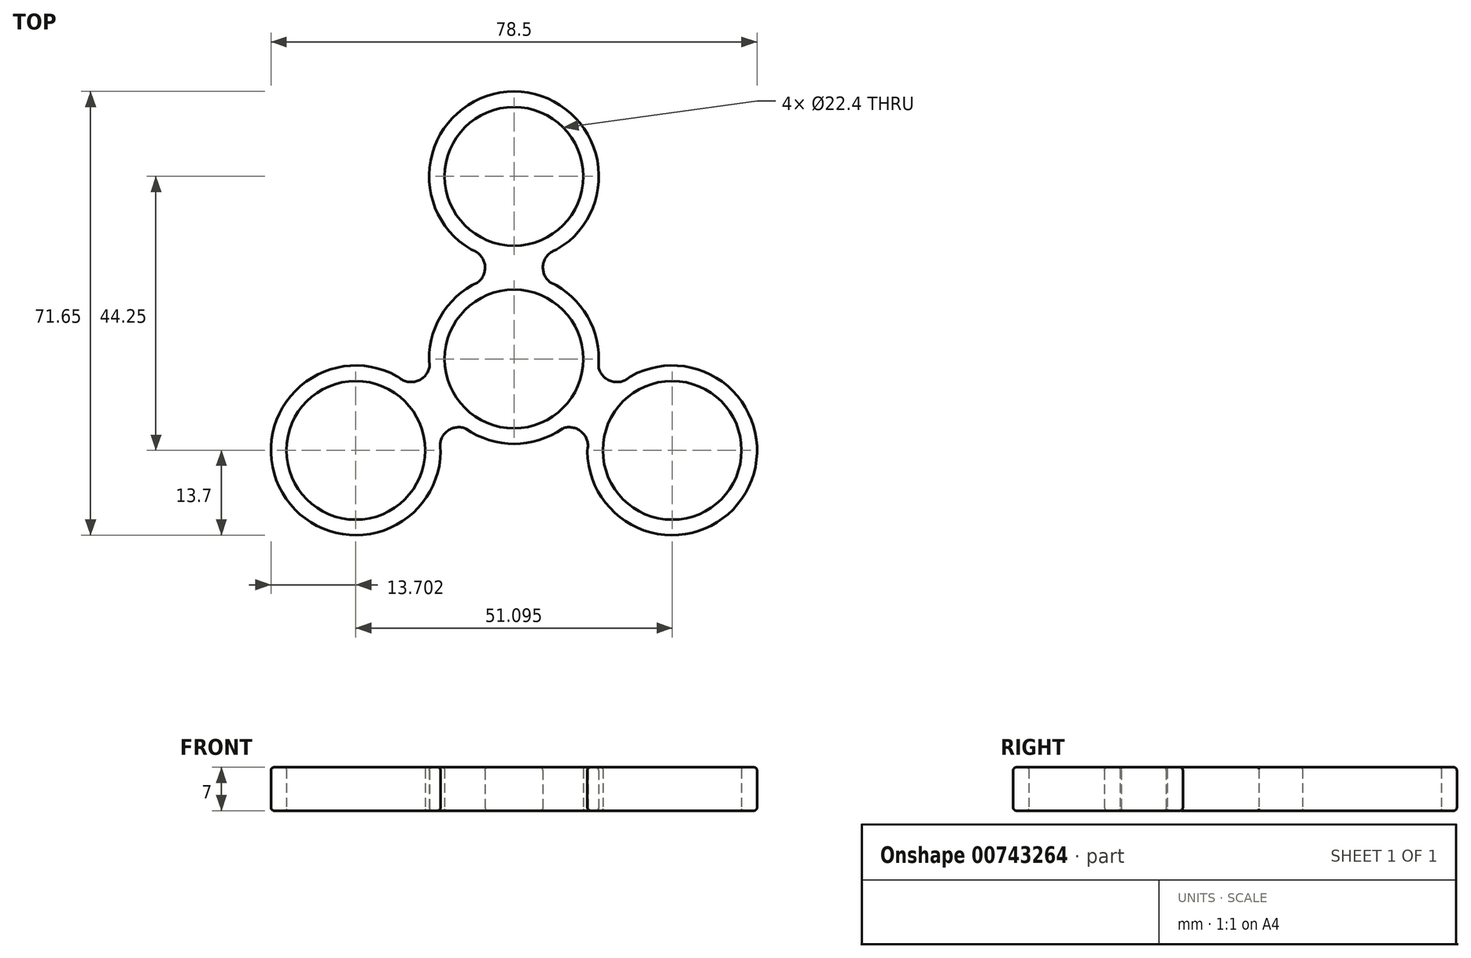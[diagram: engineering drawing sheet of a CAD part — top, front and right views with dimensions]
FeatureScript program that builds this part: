
annotation { "Feature Type Name" : "Feature", "Feature Type Description" : "" }
export const myFeature = defineFeature(function(context is Context, id is Id, definition is map)
    precondition{}
    {
        {
            var Q0;
            Q0=qCreatedBy(makeId("Top.planeOp"),FACE);
            var sketch = newSketch(context, id + "F0", { "sketchPlane" : qUnion([Q0])});
            skCircle(sketch, "E0", {"center": v(0, 0) * mm, "radius": 11.2 * mm});
            skArc(sketch, "E1.0", {"start": v(-5.2, 12.68) * mm, "mid": v(-5.5, 12.55) * mm, "end": v(-5.79, 12.42) * mm, "construction": true});
            skLineSegment(sketch, "E2", {"start": v(0, 0) * mm, "end": v(0, 29.5) * mm, "construction": true});
            skCircle(sketch, "E3", {"center": v(0, 29.5) * mm, "radius": 11.2 * mm});
            skArc(sketch, "E4.0", {"start": v(7, 17.72) * mm, "mid": v(0, 43.2) * mm, "end": v(-7, 17.72) * mm});
            skPoint(sketch, "E5.visualSharp", {"position": v(0, 14.75) * mm});
            skLineSegment(sketch, "E6.0", {"start": v(7, 0) * mm, "end": v(7, 29.5) * mm, "construction": true});
            skLineSegment(sketch, "E7", {"start": v(7, 17.72) * mm, "end": v(6.5, 17.51) * mm});
            skLineSegment(sketch, "E8", {"start": v(6.5, 11.99) * mm, "end": v(7, 11.78) * mm});
            skArc(sketch, "E9.filletArc", {"start": v(6.5, 17.51) * mm, "mid": v(4.67, 14.75) * mm, "end": v(6.5, 11.99) * mm});
            skLineSegment(sketch, "E10.MirrorCS", {"start": v(-7, 17.72) * mm, "end": v(-6.5, 17.51) * mm});
            skLineSegment(sketch, "E11.MirrorCS", {"start": v(-6.5, 11.99) * mm, "end": v(-7, 11.78) * mm});
            skArc(sketch, "E12.MirrorCS", {"start": v(-6.5, 17.51) * mm, "mid": v(-4.67, 14.75) * mm, "end": v(-6.5, 11.99) * mm});
            skArc(sketch, "E13.trimOffspring", {"start": v(-7, 11.78) * mm, "mid": v(0, -13.7) * mm, "end": v(7, 11.78) * mm});
            skSolve(sketch);
        }
        {
            var Q0;
            Q0=qSketchRegion(id+"F2",true);
            var Q1;
            Q1=qSketchRegion(id+"F0",true);
            extrude(context, id + "F1", {"entities" : qUnion([Q0, Q1]), "depth" : 7 * mm, "offsetDistance" : 25 * mm});
        }
        {
            var Q0;
            Q0=qCreatedBy(makeId("Right.planeOp"),FACE);
            var sketch = newSketch(context, id + "F2", { "sketchPlane" : qUnion([Q0])});
            skLineSegment(sketch, "E14", {"start": v(0, -11.35) * mm, "end": v(0, 14.45) * mm, "construction": true});
            skSolve(sketch);
        }
        {
            var Q0;
            Q0=makeQuery(id+"F1.opExtrude","SWEPT_BODY",BODY,{"disambiguationData":[OSD([sQuery(id+"F0.wireOp",EDGE,"E0"),sQuery(id+"F0.wireOp",EDGE,"E1.0"),sQuery(id+"F0.wireOp",EDGE,"E3"),sQuery(id+"F0.wireOp",EDGE,"E4.0"),sQuery(id+"F0.wireOp",EDGE,"7c884c8c-e37f-41f7-9a8e-9150e4511ce8.0"),sQuery(id+"F0.wireOp",EDGE,"124d70be-8a2f-4ff1-8067-023c3a760d13.0"),sQuery(id+"F0.wireOp",EDGE,"7qioyo7K-iHsX-Xa6s-X97m-BwtuQXfGrCvp"),sQuery(id+"F0.wireOp",EDGE,"oFAU7C9Q-nsB6-dseo-MMuZ-7hNLlDQCrwbt"),sQuery(id+"F0.wireOp",EDGE,"a2486781-22df-47b1-8026-fe576fbc433f.0"),sQuery(id+"F0.wireOp",EDGE,"cb9c9ce2-17e4-408e-8bf5-b38f411324f0.0"),sQuery(id+"F0.wireOp",EDGE,"jKmUo85i-UXFQ-YKQP-mafa-QPdGbBQ2pSZu"),sQuery(id+"F0.wireOp",EDGE,"14rnQz0T-OoW9-SuH9-BmvN-4Fd0IeYT7QfG")])]});
            var Q1;
            Q1=sQuery(id+"F2.wireOp",EDGE,"E14");
            circularPattern(context, id + "F3", {"operationType" : NewBodyOperationType.ADD, "entities" : qUnion([Q0]), "axis" : qUnion([Q1]), "angle" : 360 * degree, "instanceCount" : 3, "equalSpace" : true});
        }
        {
            var Q0;
            {var subQ0=makeQuery(id+"F1.opExtrude","SWEPT_FACE",FACE,{"disambiguationData":[OSD([sQuery(id+"F0.wireOp",EDGE,"E13.trimOffspring")])]});Q0=makeQuery(id+"F3.boolean.opBoolean","MERGE",FACE,{"disambiguationData":[OD(1.0)],"derivedFrom":[subQ0,makeQuery(id+"F3.opPattern","COPY",FACE,{"derivedFrom":subQ0,"instanceName":"1"}),makeQuery(id+"F3.opPattern","COPY",FACE,{"derivedFrom":subQ0,"instanceName":"2"})]});}
            var Q1;
            Q1=makeQuery(id+"F3.opPattern","COPY",FACE,{"derivedFrom":makeQuery(id+"F1.opExtrude","SWEPT_FACE",FACE,{"disambiguationData":[OSD([sQuery(id+"F0.wireOp",EDGE,"E4.0")])]}),"instanceName":"1"});
            var Q2;
            Q2=makeQuery(id+"F3.boolean.opBoolean","SPLIT",FACE,{"derivedFrom":makeQuery(id+"F1.opExtrude","SWEPT_FACE",FACE,{"disambiguationData":[OSD([sQuery(id+"F0.wireOp",EDGE,"E13.trimOffspring")])]})});
            var Q3;
            Q3=makeQuery(id+"F3.opPattern","COPY",FACE,{"derivedFrom":makeQuery(id+"F1.opExtrude","SWEPT_FACE",FACE,{"disambiguationData":[OSD([sQuery(id+"F0.wireOp",EDGE,"E12.MirrorCS")])]}),"instanceName":"1"});
            var Q4;
            Q4=makeQuery(id+"F3.opPattern","COPY",FACE,{"derivedFrom":makeQuery(id+"F1.opExtrude","SWEPT_FACE",FACE,{"disambiguationData":[OSD([sQuery(id+"F0.wireOp",EDGE,"E9.filletArc")])]}),"instanceName":"1"});
            var Q5;
            Q5=makeQuery(id+"F3.opPattern","COPY",FACE,{"derivedFrom":makeQuery(id+"F1.opExtrude","SWEPT_FACE",FACE,{"disambiguationData":[OSD([sQuery(id+"F0.wireOp",EDGE,"E9.filletArc")])]}),"instanceName":"2"});
            var Q6;
            Q6=makeQuery(id+"F3.opPattern","COPY",FACE,{"derivedFrom":makeQuery(id+"F1.opExtrude","SWEPT_FACE",FACE,{"disambiguationData":[OSD([sQuery(id+"F0.wireOp",EDGE,"E4.0")])]}),"instanceName":"2"});
            var Q7;
            Q7=makeQuery(id+"F3.opPattern","COPY",FACE,{"derivedFrom":makeQuery(id+"F1.opExtrude","SWEPT_FACE",FACE,{"disambiguationData":[OSD([sQuery(id+"F0.wireOp",EDGE,"E12.MirrorCS")])]}),"instanceName":"2"});
            var Q8;
            {var subQ0=makeQuery(id+"F1.opExtrude","SWEPT_FACE",FACE,{"disambiguationData":[OSD([sQuery(id+"F0.wireOp",EDGE,"E13.trimOffspring")])]});Q8=makeQuery(id+"F3.boolean.opBoolean","MERGE",FACE,{"disambiguationData":[OD(0.0)],"derivedFrom":[subQ0,makeQuery(id+"F3.opPattern","COPY",FACE,{"derivedFrom":subQ0,"instanceName":"1"}),makeQuery(id+"F3.opPattern","COPY",FACE,{"derivedFrom":subQ0,"instanceName":"2"})]});}
            var Q9;
            Q9=makeQuery(id+"F1.opExtrude","SWEPT_FACE",FACE,{"disambiguationData":[OSD([sQuery(id+"F0.wireOp",EDGE,"E9.filletArc")])]});
            var Q10;
            Q10=makeQuery(id+"F1.opExtrude","SWEPT_FACE",FACE,{"disambiguationData":[OSD([sQuery(id+"F0.wireOp",EDGE,"E4.0")])]});
            var Q11;
            Q11=makeQuery(id+"F1.opExtrude","SWEPT_FACE",FACE,{"disambiguationData":[OSD([sQuery(id+"F0.wireOp",EDGE,"E12.MirrorCS")])]});
            fillet(context, id + "F4", {"entities" : qUnion([Q0, Q1, Q2, Q3, Q4, Q5, Q6, Q7, Q8, Q9, Q10, Q11]), "radius" : 0.5 * mm, "tangentPropagation" : true, "allowEdgeOverflow" : false});
        }
        {
            var Q0;
            Q0=makeQuery(id+"F1.opExtrude","SWEPT_FACE",FACE,{"disambiguationData":[OSD([sQuery(id+"F0.wireOp",EDGE,"E3")])]});
            var Q1;
            Q1=makeQuery(id+"F1.opExtrude","SWEPT_FACE",FACE,{"disambiguationData":[OSD([sQuery(id+"F0.wireOp",EDGE,"E0")])]});
            var Q2;
            Q2=makeQuery(id+"F3.opPattern","COPY",FACE,{"derivedFrom":makeQuery(id+"F1.opExtrude","SWEPT_FACE",FACE,{"disambiguationData":[OSD([sQuery(id+"F0.wireOp",EDGE,"E3")])]}),"instanceName":"2"});
            var Q3;
            Q3=makeQuery(id+"F3.opPattern","COPY",FACE,{"derivedFrom":makeQuery(id+"F1.opExtrude","SWEPT_FACE",FACE,{"disambiguationData":[OSD([sQuery(id+"F0.wireOp",EDGE,"E3")])]}),"instanceName":"1"});
            fillet(context, id + "F5", {"entities" : qUnion([Q0, Q1, Q2, Q3]), "radius" : 0.3 * mm, "tangentPropagation" : true, "allowEdgeOverflow" : false});
        }
    });
